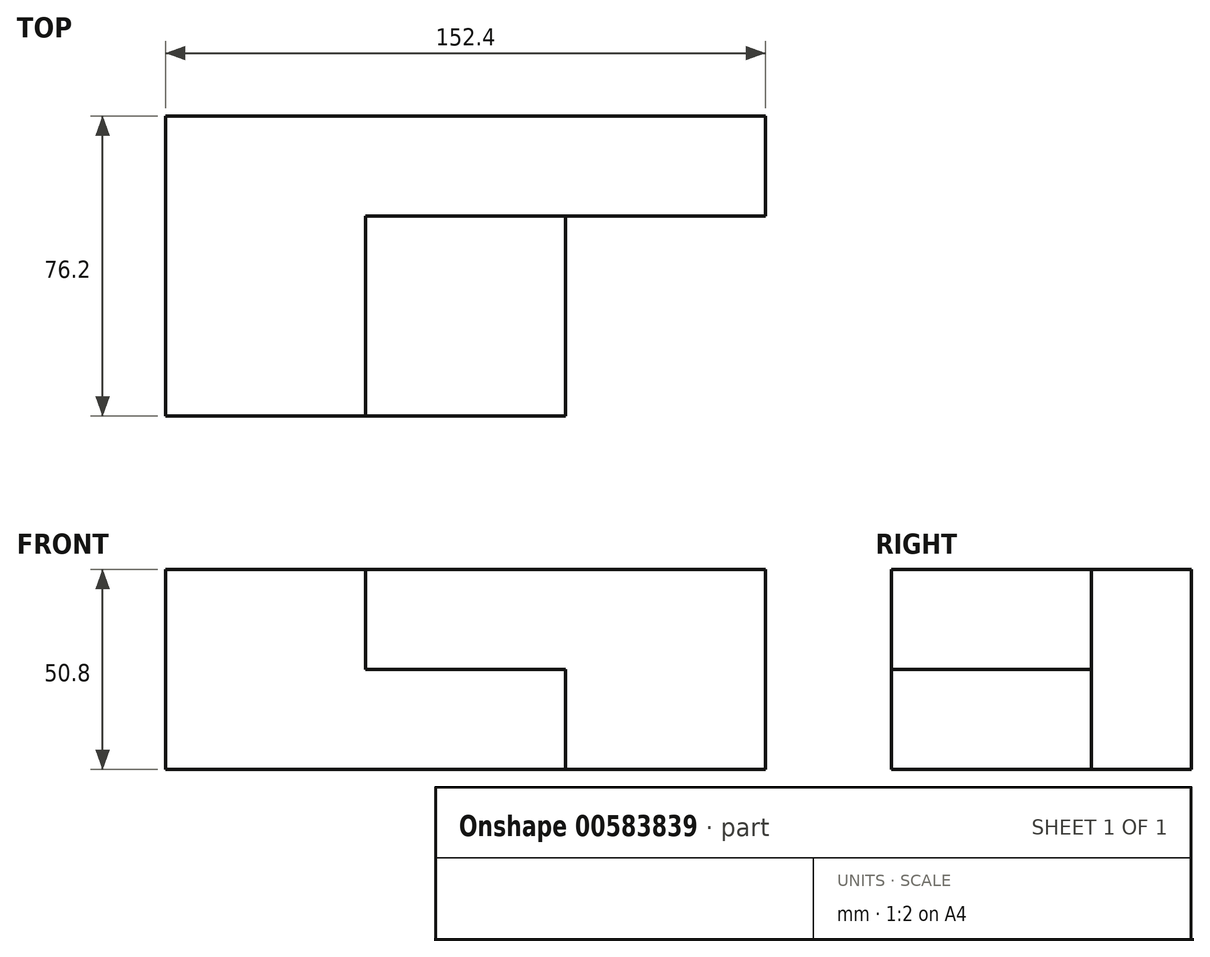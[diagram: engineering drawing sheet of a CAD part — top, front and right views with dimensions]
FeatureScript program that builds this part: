
annotation { "Feature Type Name" : "Feature", "Feature Type Description" : "" }
export const myFeature = defineFeature(function(context is Context, id is Id, definition is map)
    precondition{}
    {
        {
            var Q0;
            Q0=qCreatedBy(makeId("Top.planeOp"),FACE);
            var sketch = newSketch(context, id + "F0", { "sketchPlane" : qUnion([Q0])});
            skLineSegment(sketch, "E0.bottom", {"start": v(-133.61, 33.2) * mm, "end": v(-32.01, 33.2) * mm});
            skLineSegment(sketch, "E0.top", {"start": v(-133.61, -43) * mm, "end": v(-32.01, -43) * mm});
            skLineSegment(sketch, "E0.left", {"start": v(-133.61, 33.2) * mm, "end": v(-133.61, -43) * mm});
            skLineSegment(sketch, "E0.right", {"start": v(-32.01, 7.8) * mm, "end": v(-32.01, -43) * mm});
            skLineSegment(sketch, "E1", {"start": v(-133.61, -43) * mm, "end": v(-82.81, -43) * mm});
            skLineSegment(sketch, "E2.bottom", {"start": v(-82.81, 7.8) * mm, "end": v(-32.01, 7.8) * mm});
            skLineSegment(sketch, "E2.top", {"start": v(-82.81, -43) * mm, "end": v(-32.01, -43) * mm});
            skLineSegment(sketch, "E2.left", {"start": v(-82.81, 7.8) * mm, "end": v(-82.81, -43) * mm});
            skLineSegment(sketch, "E3.bottom", {"start": v(-32.01, 33.2) * mm, "end": v(18.79, 33.2) * mm});
            skLineSegment(sketch, "E3.top", {"start": v(-32.01, 7.8) * mm, "end": v(18.79, 7.8) * mm});
            skLineSegment(sketch, "E3.right", {"start": v(18.79, 33.2) * mm, "end": v(18.79, 7.8) * mm});
            skSolve(sketch);
        }
        {
            var Q0;
            Q0=makeQuery(id+"F0.imprint","IMPRINT",FACE,{"disambiguationData":[TD([[makeQuery(id+"F0.imprint","IMPRINT",EDGE,{"derivedFrom":sQuery(id+"F0.wireOp",EDGE,"E2.bottom")}),-1.0]])]});
            extrude(context, id + "F1", {"entities" : qUnion([Q0]), "depth" : 25.4 * mm, "offsetDistance" : 25.4 * mm});
        }
        {
            var Q0;
            Q0=makeQuery(id+"F0.imprint","IMPRINT",FACE,{"disambiguationData":[TD([[makeQuery(id+"F0.imprint","IMPRINT",EDGE,{"derivedFrom":sQuery(id+"F0.wireOp",EDGE,"E0.bottom")}),-1.0]])]});
            extrude(context, id + "F2", {"entities" : qUnion([Q0]), "operationType" : NewBodyOperationType.ADD, "depth" : 50.8 * mm, "offsetDistance" : 25.4 * mm});
        }
    });
